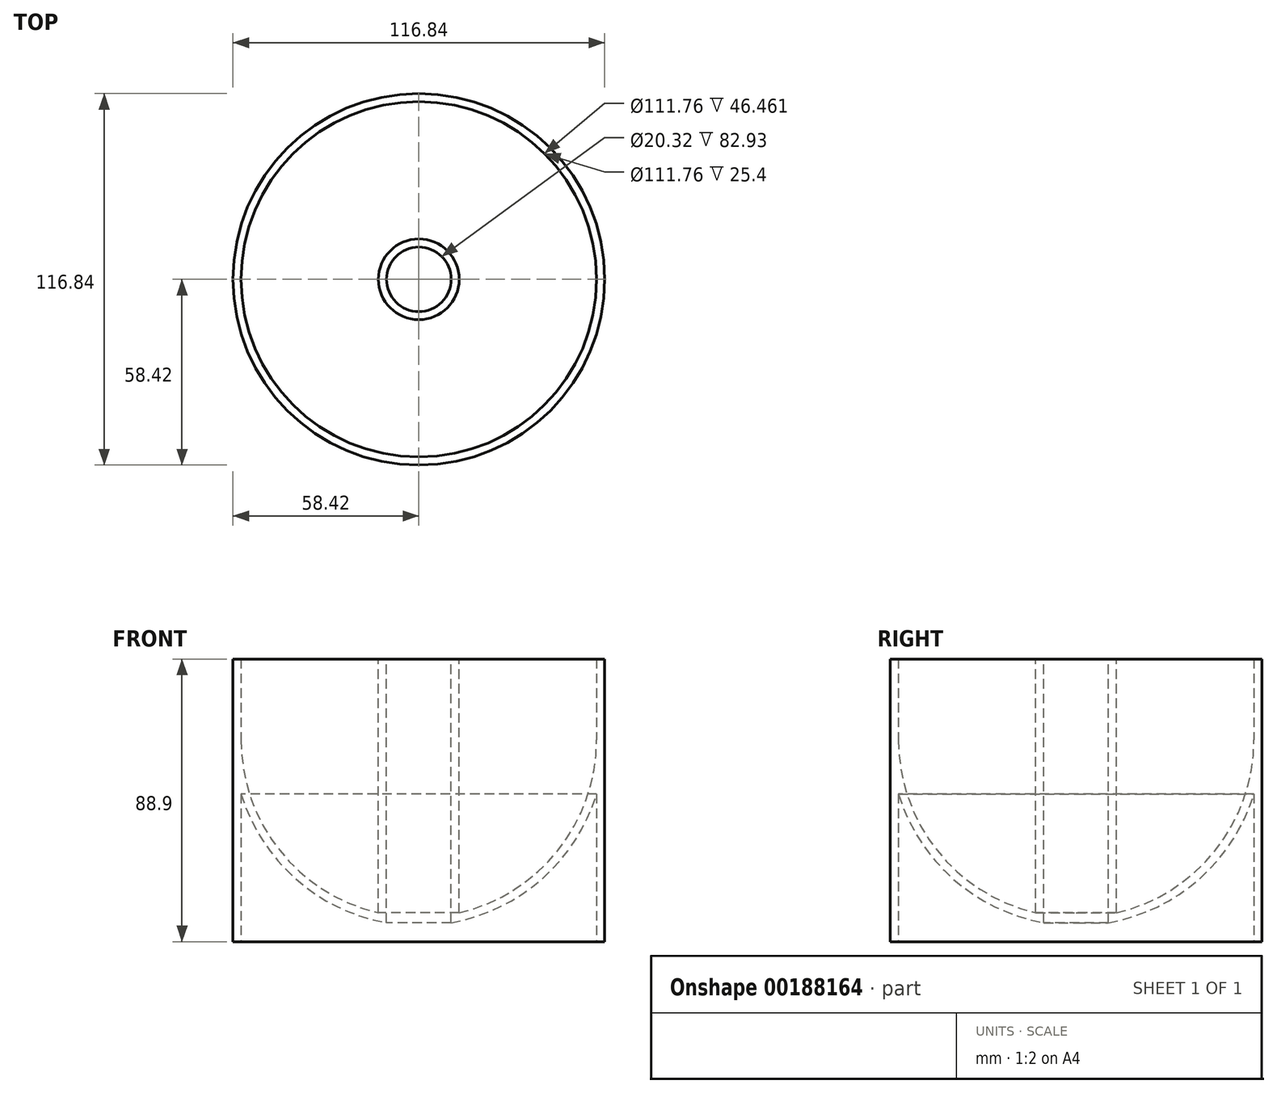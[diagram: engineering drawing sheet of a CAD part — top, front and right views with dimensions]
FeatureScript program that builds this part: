
annotation { "Feature Type Name" : "Feature", "Feature Type Description" : "" }
export const myFeature = defineFeature(function(context is Context, id is Id, definition is map)
    precondition{}
    {
        {
            var Q0;
            Q0=qCreatedBy(makeId("Top.planeOp"),FACE);
            var sketch = newSketch(context, id + "F0", { "sketchPlane" : qUnion([Q0])});
            skCircle(sketch, "E0", {"center": v(0, 0) * mm, "radius": 58.42 * mm});
            skSolve(sketch);
        }
        {
            var Q0;
            Q0 = qSketchRegion(id + "F0", true);
            extrude(context, id + "F1", {"entities" : qUnion([Q0]), "depth" : 63.5 * mm});
        }
        {
            var Q0;
            Q0=makeQuery(id+"F1.opExtrude","CAP_FACE",FACE,{"disambiguationData":[OSD([sQuery(id+"F0.wireOp",EDGE,"E0")])],"isStart":false});
            var sketch = newSketch(context, id + "F2", { "sketchPlane" : qUnion([Q0])});
            skCircle(sketch, "E1.0.0", {"center": v(0, 0) * mm, "radius": 58.42 * mm});
            skArc(sketch, "E2", {"start": v(0, 55.88) * mm, "mid": v(-55.88, 0) * mm, "end": v(0, -55.88) * mm});
            skLineSegment(sketch, "E3", {"start": v(0, 55.88) * mm, "end": v(0, -55.88) * mm});
            skSolve(sketch);
        }
        {
            var Q0;
            Q0=makeQuery(id+"F2.imprint","IMPRINT",FACE,{"disambiguationData":[TD([[makeQuery(id+"F2.imprint","IMPRINT",EDGE,{"derivedFrom":sQuery(id+"F2.wireOp",EDGE,"E2")}),1.0]])]});
            var Q1;
            Q1=sQuery(id+"F2.wireOp",EDGE,"E3");
            revolve(context, id + "F3", {"operationType" : NewBodyOperationType.REMOVE, "entities" : qUnion([Q0]), "axis" : qUnion([Q1]), "revolveType" : RevolveType.FULL, "oppositeDirection" : true});
        }
        {
            var Q0;
            Q0=makeQuery(id+"F1.opExtrude","CAP_FACE",FACE,{"disambiguationData":[OSD([sQuery(id+"F0.wireOp",EDGE,"E0")])],"isStart":true});
            shell(context, id + "F4", {"entities" : qUnion([Q0]), "thickness" : 2.54 * mm});
        }
        {
            var Q0;
            Q0=makeQuery(id+"F1.opExtrude","CAP_FACE",FACE,{"disambiguationData":[OSD([sQuery(id+"F0.wireOp",EDGE,"E0")])],"isStart":false});
            var sketch = newSketch(context, id + "F5", { "sketchPlane" : qUnion([Q0])});
            skCircle(sketch, "E4", {"center": v(0, 0) * mm, "radius": 12.7 * mm});
            skCircle(sketch, "E5", {"center": v(0, 0) * mm, "radius": 10.16 * mm});
            skSolve(sketch);
        }
        {
            var Q0;
            Q0=makeQuery(id+"F5.imprint","IMPRINT",FACE,{"disambiguationData":[TD([[makeQuery(id+"F5.imprint","IMPRINT",EDGE,{"derivedFrom":sQuery(id+"F5.wireOp",EDGE,"E4")}),1.0]])]});
            extrude(context, id + "F6", {"entities" : qUnion([Q0]), "operationType" : NewBodyOperationType.ADD, "oppositeDirection" : true, "depth" : 55.88 * mm});
        }
        {
            var Q0;
            Q0=makeQuery(id+"F6.opExtrude","CAP_FACE",FACE,{"disambiguationData":[OSD([sQuery(id+"F5.wireOp",EDGE,"E4"),sQuery(id+"F5.wireOp",EDGE,"E5")])],"isStart":true});
            var sketch = newSketch(context, id + "F7", { "sketchPlane" : qUnion([Q0])});
            skCircle(sketch, "E6.0", {"center": v(0, 0) * mm, "radius": 10.16 * mm});
            skSolve(sketch);
        }
        {
            var Q0;
            Q0 = qSketchRegion(id + "F7", true);
            extrude(context, id + "F8", {"entities" : qUnion([Q0]), "operationType" : NewBodyOperationType.REMOVE, "endBound" : BoundingType.THROUGH_ALL, "oppositeDirection" : true, "depth" : 25.4 * mm});
        }
        {
            var Q0;
            Q0=makeQuery(id+"F1.opExtrude","CAP_FACE",FACE,{"disambiguationData":[OSD([sQuery(id+"F0.wireOp",EDGE,"E0")])],"isStart":false});
            var sketch = newSketch(context, id + "F9", { "sketchPlane" : qUnion([Q0])});
            skCircle(sketch, "E7.0", {"center": v(0, 0) * mm, "radius": 58.42 * mm});
            skCircle(sketch, "E8.0", {"center": v(0, 0) * mm, "radius": 55.88 * mm});
            skSolve(sketch);
        }
        {
            var Q0;
            Q0=makeQuery(id+"F9.imprint","IMPRINT",FACE,{"disambiguationData":[TD([[makeQuery(id+"F9.imprint","IMPRINT",EDGE,{"derivedFrom":sQuery(id+"F9.wireOp",EDGE,"E7.0")}),1.0]])]});
            extrude(context, id + "F10", {"entities" : qUnion([Q0]), "operationType" : NewBodyOperationType.ADD, "depth" : 25.4 * mm});
        }
        {
            var Q0;
            Q0=makeQuery(id+"F6.opExtrude","CAP_FACE",FACE,{"disambiguationData":[OSD([sQuery(id+"F5.wireOp",EDGE,"E4"),sQuery(id+"F5.wireOp",EDGE,"E5")])],"isStart":true});
            var sketch = newSketch(context, id + "F11", { "sketchPlane" : qUnion([Q0])});
            skCircle(sketch, "E9.0", {"center": v(0, 0) * mm, "radius": 10.16 * mm});
            skCircle(sketch, "E10.0", {"center": v(0, 0) * mm, "radius": 12.7 * mm});
            skSolve(sketch);
        }
        {
            var Q0;
            Q0 = qSketchRegion(id + "F11", true);
            extrude(context, id + "F12", {"entities" : qUnion([Q0]), "operationType" : NewBodyOperationType.ADD, "depth" : 25.4 * mm});
        }
    });
